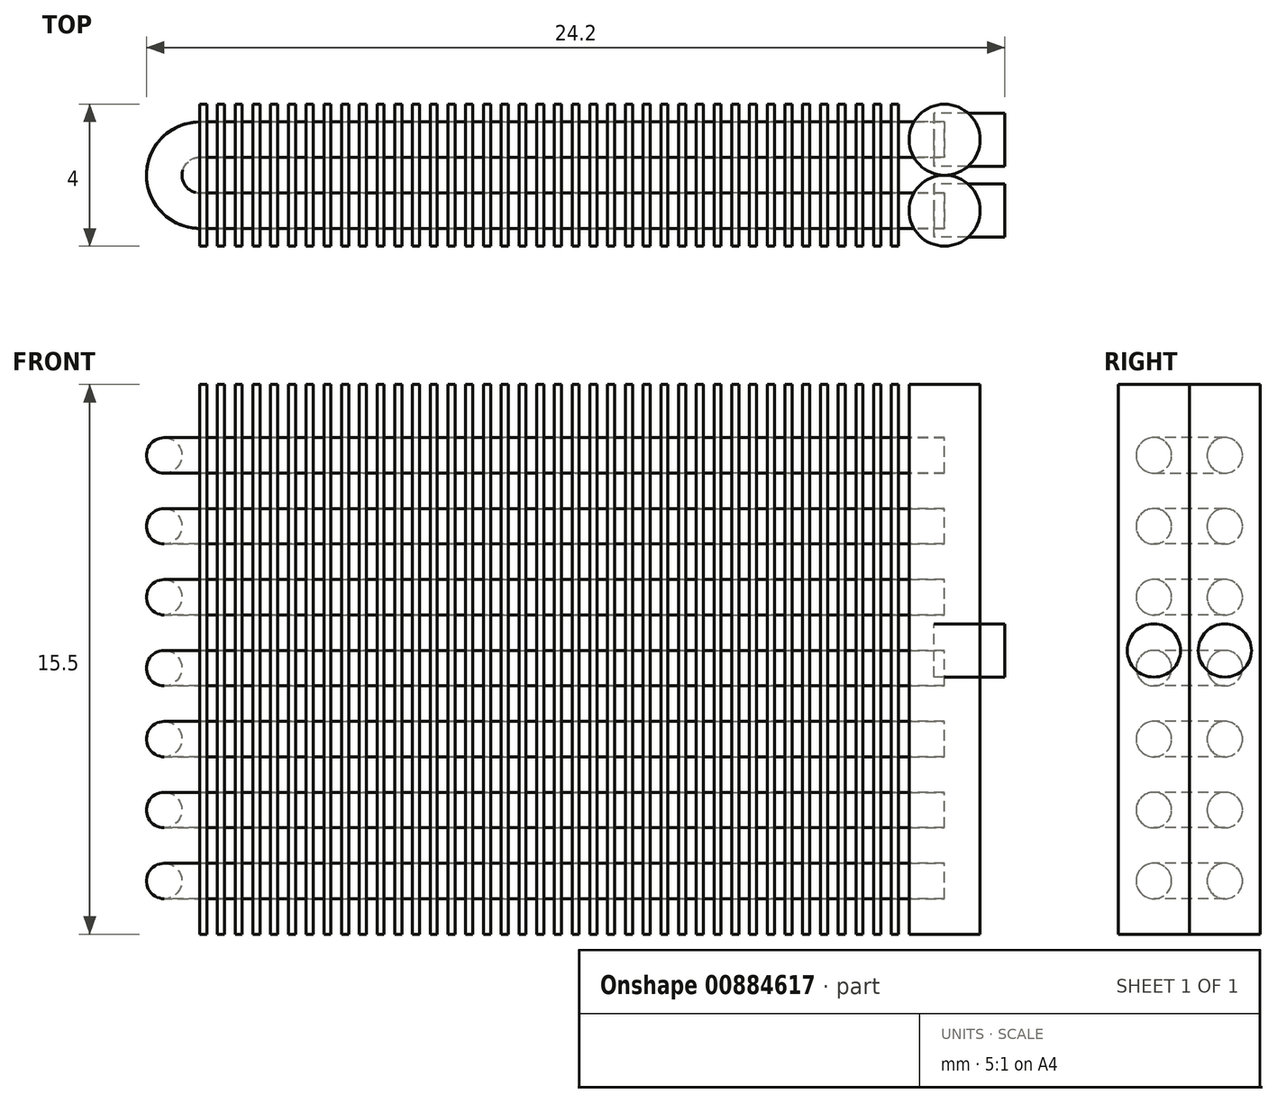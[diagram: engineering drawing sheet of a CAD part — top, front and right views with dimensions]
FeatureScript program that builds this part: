
annotation { "Feature Type Name" : "Feature", "Feature Type Description" : "" }
export const myFeature = defineFeature(function(context is Context, id is Id, definition is map)
    precondition{}
    {
        {
            var Q0;
            Q0=qCreatedBy(makeId("Top.planeOp"),FACE);
            var sketch = newSketch(context, id + "F0", { "sketchPlane" : qUnion([Q0])});
            skLineSegment(sketch, "E0.bottom", {"start": v(0, 0) * mm, "end": v(0.2, 0) * mm});
            skLineSegment(sketch, "E0.top", {"start": v(0, 4) * mm, "end": v(0.2, 4) * mm});
            skLineSegment(sketch, "E0.left", {"start": v(0, 0) * mm, "end": v(0, 4) * mm});
            skLineSegment(sketch, "E0.right", {"start": v(0.2, 0) * mm, "end": v(0.2, 4) * mm});
            skLineSegment(sketch, "E1.1.0.0", {"start": v(0.5, 0) * mm, "end": v(0.5, 4) * mm});
            skLineSegment(sketch, "E1.1.0.1", {"start": v(0.7, 0) * mm, "end": v(0.7, 4) * mm});
            skLineSegment(sketch, "E1.1.0.2", {"start": v(0.5, 4) * mm, "end": v(0.7, 4) * mm});
            skLineSegment(sketch, "E1.1.0.3", {"start": v(0.5, 0) * mm, "end": v(0.7, 0) * mm});
            skLineSegment(sketch, "E1.2.0.0", {"start": v(1, 0) * mm, "end": v(1, 4) * mm});
            skLineSegment(sketch, "E1.2.0.1", {"start": v(1.2, 0) * mm, "end": v(1.2, 4) * mm});
            skLineSegment(sketch, "E1.2.0.2", {"start": v(1, 4) * mm, "end": v(1.2, 4) * mm});
            skLineSegment(sketch, "E1.2.0.3", {"start": v(1, 0) * mm, "end": v(1.2, 0) * mm});
            skLineSegment(sketch, "E1.3.0.0", {"start": v(1.5, 0) * mm, "end": v(1.5, 4) * mm});
            skLineSegment(sketch, "E1.3.0.1", {"start": v(1.7, 0) * mm, "end": v(1.7, 4) * mm});
            skLineSegment(sketch, "E1.3.0.2", {"start": v(1.5, 4) * mm, "end": v(1.7, 4) * mm});
            skLineSegment(sketch, "E1.3.0.3", {"start": v(1.5, 0) * mm, "end": v(1.7, 0) * mm});
            skLineSegment(sketch, "E1.4.0.0", {"start": v(2, 0) * mm, "end": v(2, 4) * mm});
            skLineSegment(sketch, "E1.4.0.1", {"start": v(2.2, 0) * mm, "end": v(2.2, 4) * mm});
            skLineSegment(sketch, "E1.4.0.2", {"start": v(2, 4) * mm, "end": v(2.2, 4) * mm});
            skLineSegment(sketch, "E1.4.0.3", {"start": v(2, 0) * mm, "end": v(2.2, 0) * mm});
            skLineSegment(sketch, "E1.5.0.0", {"start": v(2.5, 0) * mm, "end": v(2.5, 4) * mm});
            skLineSegment(sketch, "E1.5.0.1", {"start": v(2.7, 0) * mm, "end": v(2.7, 4) * mm});
            skLineSegment(sketch, "E1.5.0.2", {"start": v(2.5, 4) * mm, "end": v(2.7, 4) * mm});
            skLineSegment(sketch, "E1.5.0.3", {"start": v(2.5, 0) * mm, "end": v(2.7, 0) * mm});
            skLineSegment(sketch, "E1.6.0.0", {"start": v(3, 0) * mm, "end": v(3, 4) * mm});
            skLineSegment(sketch, "E1.6.0.1", {"start": v(3.2, 0) * mm, "end": v(3.2, 4) * mm});
            skLineSegment(sketch, "E1.6.0.2", {"start": v(3, 4) * mm, "end": v(3.2, 4) * mm});
            skLineSegment(sketch, "E1.6.0.3", {"start": v(3, 0) * mm, "end": v(3.2, 0) * mm});
            skLineSegment(sketch, "E1.7.0.0", {"start": v(3.5, 0) * mm, "end": v(3.5, 4) * mm});
            skLineSegment(sketch, "E1.7.0.1", {"start": v(3.7, 0) * mm, "end": v(3.7, 4) * mm});
            skLineSegment(sketch, "E1.7.0.2", {"start": v(3.5, 4) * mm, "end": v(3.7, 4) * mm});
            skLineSegment(sketch, "E1.7.0.3", {"start": v(3.5, 0) * mm, "end": v(3.7, 0) * mm});
            skLineSegment(sketch, "E1.8.0.0", {"start": v(4, 0) * mm, "end": v(4, 4) * mm});
            skLineSegment(sketch, "E1.8.0.1", {"start": v(4.2, 0) * mm, "end": v(4.2, 4) * mm});
            skLineSegment(sketch, "E1.8.0.2", {"start": v(4, 4) * mm, "end": v(4.2, 4) * mm});
            skLineSegment(sketch, "E1.8.0.3", {"start": v(4, 0) * mm, "end": v(4.2, 0) * mm});
            skLineSegment(sketch, "E1.9.0.0", {"start": v(4.5, 0) * mm, "end": v(4.5, 4) * mm});
            skLineSegment(sketch, "E1.9.0.1", {"start": v(4.7, 0) * mm, "end": v(4.7, 4) * mm});
            skLineSegment(sketch, "E1.9.0.2", {"start": v(4.5, 4) * mm, "end": v(4.7, 4) * mm});
            skLineSegment(sketch, "E1.9.0.3", {"start": v(4.5, 0) * mm, "end": v(4.7, 0) * mm});
            skLineSegment(sketch, "E1.10.0.0", {"start": v(5, 0) * mm, "end": v(5, 4) * mm});
            skLineSegment(sketch, "E1.10.0.1", {"start": v(5.2, 0) * mm, "end": v(5.2, 4) * mm});
            skLineSegment(sketch, "E1.10.0.2", {"start": v(5, 4) * mm, "end": v(5.2, 4) * mm});
            skLineSegment(sketch, "E1.10.0.3", {"start": v(5, 0) * mm, "end": v(5.2, 0) * mm});
            skLineSegment(sketch, "E1.11.0.0", {"start": v(5.5, 0) * mm, "end": v(5.5, 4) * mm});
            skLineSegment(sketch, "E1.11.0.1", {"start": v(5.7, 0) * mm, "end": v(5.7, 4) * mm});
            skLineSegment(sketch, "E1.11.0.2", {"start": v(5.5, 4) * mm, "end": v(5.7, 4) * mm});
            skLineSegment(sketch, "E1.11.0.3", {"start": v(5.5, 0) * mm, "end": v(5.7, 0) * mm});
            skLineSegment(sketch, "E1.12.0.0", {"start": v(6, 0) * mm, "end": v(6, 4) * mm});
            skLineSegment(sketch, "E1.12.0.1", {"start": v(6.2, 0) * mm, "end": v(6.2, 4) * mm});
            skLineSegment(sketch, "E1.12.0.2", {"start": v(6, 4) * mm, "end": v(6.2, 4) * mm});
            skLineSegment(sketch, "E1.12.0.3", {"start": v(6, 0) * mm, "end": v(6.2, 0) * mm});
            skLineSegment(sketch, "E1.13.0.0", {"start": v(6.5, 0) * mm, "end": v(6.5, 4) * mm});
            skLineSegment(sketch, "E1.13.0.1", {"start": v(6.7, 0) * mm, "end": v(6.7, 4) * mm});
            skLineSegment(sketch, "E1.13.0.2", {"start": v(6.5, 4) * mm, "end": v(6.7, 4) * mm});
            skLineSegment(sketch, "E1.13.0.3", {"start": v(6.5, 0) * mm, "end": v(6.7, 0) * mm});
            skLineSegment(sketch, "E1.14.0.0", {"start": v(7, 0) * mm, "end": v(7, 4) * mm});
            skLineSegment(sketch, "E1.14.0.1", {"start": v(7.2, 0) * mm, "end": v(7.2, 4) * mm});
            skLineSegment(sketch, "E1.14.0.2", {"start": v(7, 4) * mm, "end": v(7.2, 4) * mm});
            skLineSegment(sketch, "E1.14.0.3", {"start": v(7, 0) * mm, "end": v(7.2, 0) * mm});
            skLineSegment(sketch, "E1.15.0.0", {"start": v(7.5, 0) * mm, "end": v(7.5, 4) * mm});
            skLineSegment(sketch, "E1.15.0.1", {"start": v(7.7, 0) * mm, "end": v(7.7, 4) * mm});
            skLineSegment(sketch, "E1.15.0.2", {"start": v(7.5, 4) * mm, "end": v(7.7, 4) * mm});
            skLineSegment(sketch, "E1.15.0.3", {"start": v(7.5, 0) * mm, "end": v(7.7, 0) * mm});
            skLineSegment(sketch, "E1.16.0.0", {"start": v(8, 0) * mm, "end": v(8, 4) * mm});
            skLineSegment(sketch, "E1.16.0.1", {"start": v(8.2, 0) * mm, "end": v(8.2, 4) * mm});
            skLineSegment(sketch, "E1.16.0.2", {"start": v(8, 4) * mm, "end": v(8.2, 4) * mm});
            skLineSegment(sketch, "E1.16.0.3", {"start": v(8, 0) * mm, "end": v(8.2, 0) * mm});
            skLineSegment(sketch, "E1.17.0.0", {"start": v(8.5, 0) * mm, "end": v(8.5, 4) * mm});
            skLineSegment(sketch, "E1.17.0.1", {"start": v(8.7, 0) * mm, "end": v(8.7, 4) * mm});
            skLineSegment(sketch, "E1.17.0.2", {"start": v(8.5, 4) * mm, "end": v(8.7, 4) * mm});
            skLineSegment(sketch, "E1.17.0.3", {"start": v(8.5, 0) * mm, "end": v(8.7, 0) * mm});
            skLineSegment(sketch, "E1.18.0.0", {"start": v(9, 0) * mm, "end": v(9, 4) * mm});
            skLineSegment(sketch, "E1.18.0.1", {"start": v(9.2, 0) * mm, "end": v(9.2, 4) * mm});
            skLineSegment(sketch, "E1.18.0.2", {"start": v(9, 4) * mm, "end": v(9.2, 4) * mm});
            skLineSegment(sketch, "E1.18.0.3", {"start": v(9, 0) * mm, "end": v(9.2, 0) * mm});
            skLineSegment(sketch, "E1.19.0.0", {"start": v(9.5, 0) * mm, "end": v(9.5, 4) * mm});
            skLineSegment(sketch, "E1.19.0.1", {"start": v(9.7, 0) * mm, "end": v(9.7, 4) * mm});
            skLineSegment(sketch, "E1.19.0.2", {"start": v(9.5, 4) * mm, "end": v(9.7, 4) * mm});
            skLineSegment(sketch, "E1.19.0.3", {"start": v(9.5, 0) * mm, "end": v(9.7, 0) * mm});
            skLineSegment(sketch, "E1.20.0.0", {"start": v(10, 0) * mm, "end": v(10, 4) * mm});
            skLineSegment(sketch, "E1.20.0.1", {"start": v(10.2, 0) * mm, "end": v(10.2, 4) * mm});
            skLineSegment(sketch, "E1.20.0.2", {"start": v(10, 4) * mm, "end": v(10.2, 4) * mm});
            skLineSegment(sketch, "E1.20.0.3", {"start": v(10, 0) * mm, "end": v(10.2, 0) * mm});
            skLineSegment(sketch, "E1.21.0.0", {"start": v(10.5, 0) * mm, "end": v(10.5, 4) * mm});
            skLineSegment(sketch, "E1.21.0.1", {"start": v(10.7, 0) * mm, "end": v(10.7, 4) * mm});
            skLineSegment(sketch, "E1.21.0.2", {"start": v(10.5, 4) * mm, "end": v(10.7, 4) * mm});
            skLineSegment(sketch, "E1.21.0.3", {"start": v(10.5, 0) * mm, "end": v(10.7, 0) * mm});
            skLineSegment(sketch, "E1.22.0.0", {"start": v(11, 0) * mm, "end": v(11, 4) * mm});
            skLineSegment(sketch, "E1.22.0.1", {"start": v(11.2, 0) * mm, "end": v(11.2, 4) * mm});
            skLineSegment(sketch, "E1.22.0.2", {"start": v(11, 4) * mm, "end": v(11.2, 4) * mm});
            skLineSegment(sketch, "E1.22.0.3", {"start": v(11, 0) * mm, "end": v(11.2, 0) * mm});
            skLineSegment(sketch, "E1.23.0.0", {"start": v(11.5, 0) * mm, "end": v(11.5, 4) * mm});
            skLineSegment(sketch, "E1.23.0.1", {"start": v(11.7, 0) * mm, "end": v(11.7, 4) * mm});
            skLineSegment(sketch, "E1.23.0.2", {"start": v(11.5, 4) * mm, "end": v(11.7, 4) * mm});
            skLineSegment(sketch, "E1.23.0.3", {"start": v(11.5, 0) * mm, "end": v(11.7, 0) * mm});
            skLineSegment(sketch, "E1.24.0.0", {"start": v(12, 0) * mm, "end": v(12, 4) * mm});
            skLineSegment(sketch, "E1.24.0.1", {"start": v(12.2, 0) * mm, "end": v(12.2, 4) * mm});
            skLineSegment(sketch, "E1.24.0.2", {"start": v(12, 4) * mm, "end": v(12.2, 4) * mm});
            skLineSegment(sketch, "E1.24.0.3", {"start": v(12, 0) * mm, "end": v(12.2, 0) * mm});
            skLineSegment(sketch, "E1.25.0.0", {"start": v(12.5, 0) * mm, "end": v(12.5, 4) * mm});
            skLineSegment(sketch, "E1.25.0.1", {"start": v(12.7, 0) * mm, "end": v(12.7, 4) * mm});
            skLineSegment(sketch, "E1.25.0.2", {"start": v(12.5, 4) * mm, "end": v(12.7, 4) * mm});
            skLineSegment(sketch, "E1.25.0.3", {"start": v(12.5, 0) * mm, "end": v(12.7, 0) * mm});
            skLineSegment(sketch, "E1.26.0.0", {"start": v(13, 0) * mm, "end": v(13, 4) * mm});
            skLineSegment(sketch, "E1.26.0.1", {"start": v(13.2, 0) * mm, "end": v(13.2, 4) * mm});
            skLineSegment(sketch, "E1.26.0.2", {"start": v(13, 4) * mm, "end": v(13.2, 4) * mm});
            skLineSegment(sketch, "E1.26.0.3", {"start": v(13, 0) * mm, "end": v(13.2, 0) * mm});
            skLineSegment(sketch, "E1.27.0.0", {"start": v(13.5, 0) * mm, "end": v(13.5, 4) * mm});
            skLineSegment(sketch, "E1.27.0.1", {"start": v(13.7, 0) * mm, "end": v(13.7, 4) * mm});
            skLineSegment(sketch, "E1.27.0.2", {"start": v(13.5, 4) * mm, "end": v(13.7, 4) * mm});
            skLineSegment(sketch, "E1.27.0.3", {"start": v(13.5, 0) * mm, "end": v(13.7, 0) * mm});
            skLineSegment(sketch, "E1.28.0.0", {"start": v(14, 0) * mm, "end": v(14, 4) * mm});
            skLineSegment(sketch, "E1.28.0.1", {"start": v(14.2, 0) * mm, "end": v(14.2, 4) * mm});
            skLineSegment(sketch, "E1.28.0.2", {"start": v(14, 4) * mm, "end": v(14.2, 4) * mm});
            skLineSegment(sketch, "E1.28.0.3", {"start": v(14, 0) * mm, "end": v(14.2, 0) * mm});
            skLineSegment(sketch, "E1.29.0.0", {"start": v(14.5, 0) * mm, "end": v(14.5, 4) * mm});
            skLineSegment(sketch, "E1.29.0.1", {"start": v(14.7, 0) * mm, "end": v(14.7, 4) * mm});
            skLineSegment(sketch, "E1.29.0.2", {"start": v(14.5, 4) * mm, "end": v(14.7, 4) * mm});
            skLineSegment(sketch, "E1.29.0.3", {"start": v(14.5, 0) * mm, "end": v(14.7, 0) * mm});
            skLineSegment(sketch, "E1.30.0.0", {"start": v(15, 0) * mm, "end": v(15, 4) * mm});
            skLineSegment(sketch, "E1.30.0.1", {"start": v(15.2, 0) * mm, "end": v(15.2, 4) * mm});
            skLineSegment(sketch, "E1.30.0.2", {"start": v(15, 4) * mm, "end": v(15.2, 4) * mm});
            skLineSegment(sketch, "E1.30.0.3", {"start": v(15, 0) * mm, "end": v(15.2, 0) * mm});
            skLineSegment(sketch, "E1.31.0.0", {"start": v(15.5, 0) * mm, "end": v(15.5, 4) * mm});
            skLineSegment(sketch, "E1.31.0.1", {"start": v(15.7, 0) * mm, "end": v(15.7, 4) * mm});
            skLineSegment(sketch, "E1.31.0.2", {"start": v(15.5, 4) * mm, "end": v(15.7, 4) * mm});
            skLineSegment(sketch, "E1.31.0.3", {"start": v(15.5, 0) * mm, "end": v(15.7, 0) * mm});
            skLineSegment(sketch, "E1.32.0.0", {"start": v(16, 0) * mm, "end": v(16, 4) * mm});
            skLineSegment(sketch, "E1.32.0.1", {"start": v(16.2, 0) * mm, "end": v(16.2, 4) * mm});
            skLineSegment(sketch, "E1.32.0.2", {"start": v(16, 4) * mm, "end": v(16.2, 4) * mm});
            skLineSegment(sketch, "E1.32.0.3", {"start": v(16, 0) * mm, "end": v(16.2, 0) * mm});
            skLineSegment(sketch, "E1.33.0.0", {"start": v(16.5, 0) * mm, "end": v(16.5, 4) * mm});
            skLineSegment(sketch, "E1.33.0.1", {"start": v(16.7, 0) * mm, "end": v(16.7, 4) * mm});
            skLineSegment(sketch, "E1.33.0.2", {"start": v(16.5, 4) * mm, "end": v(16.7, 4) * mm});
            skLineSegment(sketch, "E1.33.0.3", {"start": v(16.5, 0) * mm, "end": v(16.7, 0) * mm});
            skLineSegment(sketch, "E1.34.0.0", {"start": v(17, 0) * mm, "end": v(17, 4) * mm});
            skLineSegment(sketch, "E1.34.0.1", {"start": v(17.2, 0) * mm, "end": v(17.2, 4) * mm});
            skLineSegment(sketch, "E1.34.0.2", {"start": v(17, 4) * mm, "end": v(17.2, 4) * mm});
            skLineSegment(sketch, "E1.34.0.3", {"start": v(17, 0) * mm, "end": v(17.2, 0) * mm});
            skLineSegment(sketch, "E1.35.0.0", {"start": v(17.5, 0) * mm, "end": v(17.5, 4) * mm});
            skLineSegment(sketch, "E1.35.0.1", {"start": v(17.7, 0) * mm, "end": v(17.7, 4) * mm});
            skLineSegment(sketch, "E1.35.0.2", {"start": v(17.5, 4) * mm, "end": v(17.7, 4) * mm});
            skLineSegment(sketch, "E1.35.0.3", {"start": v(17.5, 0) * mm, "end": v(17.7, 0) * mm});
            skLineSegment(sketch, "E1.36.0.0", {"start": v(18, 0) * mm, "end": v(18, 4) * mm});
            skLineSegment(sketch, "E1.36.0.1", {"start": v(18.2, 0) * mm, "end": v(18.2, 4) * mm});
            skLineSegment(sketch, "E1.36.0.2", {"start": v(18, 4) * mm, "end": v(18.2, 4) * mm});
            skLineSegment(sketch, "E1.36.0.3", {"start": v(18, 0) * mm, "end": v(18.2, 0) * mm});
            skLineSegment(sketch, "E1.37.0.0", {"start": v(18.5, 0) * mm, "end": v(18.5, 4) * mm});
            skLineSegment(sketch, "E1.37.0.1", {"start": v(18.7, 0) * mm, "end": v(18.7, 4) * mm});
            skLineSegment(sketch, "E1.37.0.2", {"start": v(18.5, 4) * mm, "end": v(18.7, 4) * mm});
            skLineSegment(sketch, "E1.37.0.3", {"start": v(18.5, 0) * mm, "end": v(18.7, 0) * mm});
            skLineSegment(sketch, "E1.38.0.0", {"start": v(19, 0) * mm, "end": v(19, 4) * mm});
            skLineSegment(sketch, "E1.38.0.1", {"start": v(19.2, 0) * mm, "end": v(19.2, 4) * mm});
            skLineSegment(sketch, "E1.38.0.2", {"start": v(19, 4) * mm, "end": v(19.2, 4) * mm});
            skLineSegment(sketch, "E1.38.0.3", {"start": v(19, 0) * mm, "end": v(19.2, 0) * mm});
            skLineSegment(sketch, "E1.39.0.0", {"start": v(19.5, 0) * mm, "end": v(19.5, 4) * mm});
            skLineSegment(sketch, "E1.39.0.1", {"start": v(19.7, 0) * mm, "end": v(19.7, 4) * mm});
            skLineSegment(sketch, "E1.39.0.2", {"start": v(19.5, 4) * mm, "end": v(19.7, 4) * mm});
            skLineSegment(sketch, "E1.39.0.3", {"start": v(19.5, 0) * mm, "end": v(19.7, 0) * mm});
            skLineSegment(sketch, "E1.direction1", {"start": v(0, 0) * mm, "end": v(0.5, 0) * mm, "construction": true});
            skCircle(sketch, "E2", {"center": v(21, 3) * mm, "radius": 1 * mm});
            skCircle(sketch, "E3", {"center": v(21, 1) * mm, "radius": 1 * mm});
            skLineSegment(sketch, "E4", {"start": v(21, 3) * mm, "end": v(21, 1) * mm, "construction": true});
            skSolve(sketch);
        }
        {
            var Q0;
            Q0 = qSketchRegion(id + "F0", true);
            extrude(context, id + "F1", {"entities" : qUnion([Q0]), "depth" : 15.5 * mm, "offsetDistance" : 25 * mm});
        }
        {
            var Q0;
            Q0=qCreatedBy(makeId("Top.planeOp"),FACE);
            var sketch = newSketch(context, id + "F2", { "sketchPlane" : qUnion([Q0])});
            skLineSegment(sketch, "E5", {"start": v(21, 1) * mm, "end": v(0, 1) * mm});
            skLineSegment(sketch, "E6", {"start": v(21, 3) * mm, "end": v(0, 3) * mm});
            skArc(sketch, "E7", {"start": v(0, 3) * mm, "mid": v(-1, 2) * mm, "end": v(0, 1) * mm});
            skSolve(sketch);
        }
        {
            var Q0;
            Q0=makeQuery(id+"F1.opExtrude","SWEPT_FACE",FACE,{"disambiguationData":[OSD([sQuery(id+"F0.wireOp",EDGE,"E1.39.0.1")])]});
            var sketch = newSketch(context, id + "F3", { "sketchPlane" : qUnion([Q0])});
            skCircle(sketch, "E8", {"center": v(1, 1.5) * mm, "radius": 0.5 * mm});
            skCircle(sketch, "E9.0.1.0", {"center": v(1, 3.5) * mm, "radius": 0.5 * mm});
            skCircle(sketch, "E9.0.2.0", {"center": v(1, 5.5) * mm, "radius": 0.5 * mm});
            skCircle(sketch, "E9.0.3.0", {"center": v(1, 7.5) * mm, "radius": 0.5 * mm});
            skCircle(sketch, "E9.0.4.0", {"center": v(1, 9.5) * mm, "radius": 0.5 * mm});
            skCircle(sketch, "E9.0.5.0", {"center": v(1, 11.5) * mm, "radius": 0.5 * mm});
            skCircle(sketch, "E9.0.6.0", {"center": v(1, 13.5) * mm, "radius": 0.5 * mm});
            skCircle(sketch, "E9.1.0.0", {"center": v(3, 1.5) * mm, "radius": 0.5 * mm});
            skCircle(sketch, "E9.1.1.0", {"center": v(3, 3.5) * mm, "radius": 0.5 * mm});
            skCircle(sketch, "E9.1.2.0", {"center": v(3, 5.5) * mm, "radius": 0.5 * mm});
            skCircle(sketch, "E9.1.3.0", {"center": v(3, 7.5) * mm, "radius": 0.5 * mm});
            skCircle(sketch, "E9.1.4.0", {"center": v(3, 9.5) * mm, "radius": 0.5 * mm});
            skCircle(sketch, "E9.1.5.0", {"center": v(3, 11.5) * mm, "radius": 0.5 * mm});
            skCircle(sketch, "E9.1.6.0", {"center": v(3, 13.5) * mm, "radius": 0.5 * mm});
            skLineSegment(sketch, "E9.direction1", {"start": v(1, 1.5) * mm, "end": v(3, 1.5) * mm, "construction": true});
            skLineSegment(sketch, "E9.direction2", {"start": v(1, 1.5) * mm, "end": v(1, 3.5) * mm, "construction": true});
            skSolve(sketch);
        }
        {
            var Q0;
            Q0 = qSketchRegion(id + "F3", true);
            var Q1;
            Q1 = qConstructionFilter(qBodyType(qCreatedBy(id + "F2" ,EDGE), BodyType.WIRE), ConstructionObject.NO);
            sweep(context, id + "F4", {"profiles" : qUnion([Q0]), "path" : qUnion([Q1])});
        }
        {
            var Q0;
            Q0=makeQuery(id+"F1.opExtrude","SWEPT_FACE",FACE,{"disambiguationData":[OSD([sQuery(id+"F0.wireOp",EDGE,"E1.39.0.1")])]});
            var sketch = newSketch(context, id + "F5", { "sketchPlane" : qUnion([Q0])});
            skCircle(sketch, "E10", {"center": v(1, 8) * mm, "radius": 0.75 * mm});
            skCircle(sketch, "E11", {"center": v(3, 8) * mm, "radius": 0.75 * mm});
            skSolve(sketch);
        }
        {
            var Q0;
            Q0 = qSketchRegion(id + "F5", true);
            extrude(context, id + "F6", {"entities" : qUnion([Q0]), "depth" : 3 * mm, "offsetDistance" : 25 * mm, "hasSecondDirection" : true, "secondDirectionOppositeDirection" : false, "secondDirectionDepth" : 1 * mm});
        }
    });
